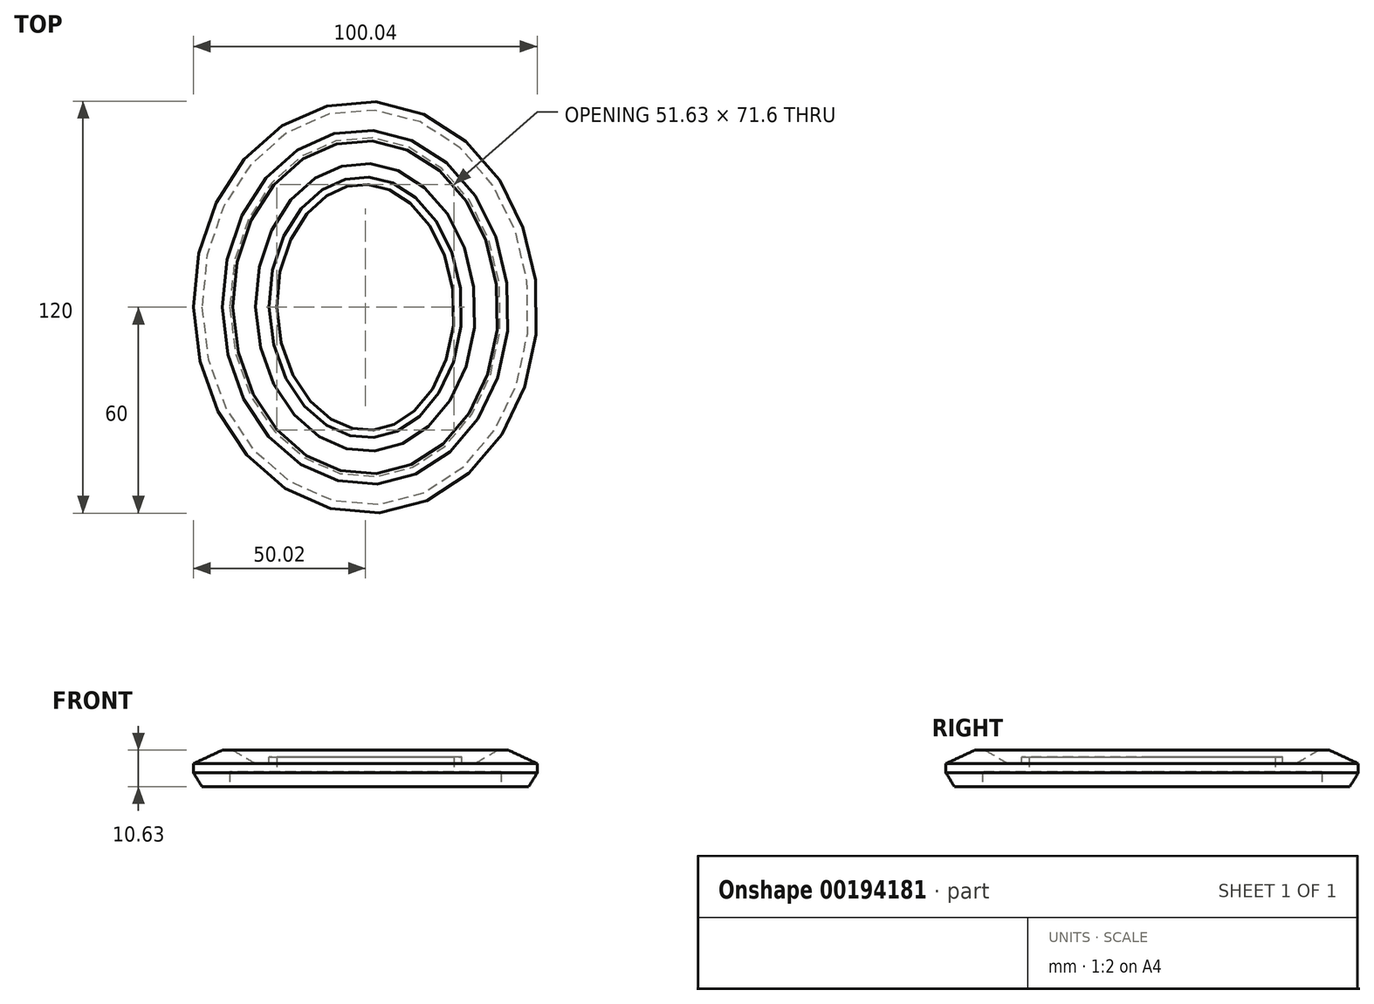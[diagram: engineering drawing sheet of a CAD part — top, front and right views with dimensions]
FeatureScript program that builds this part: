
annotation { "Feature Type Name" : "Feature", "Feature Type Description" : "" }
export const myFeature = defineFeature(function(context is Context, id is Id, definition is map)
    precondition{}
    {
        {
            var Q0;
            Q0=qCreatedBy(makeId("Front.planeOp"),FACE);
            var sketch = newSketch(context, id + "F0", { "sketchPlane" : qUnion([Q0])});
            skLineSegment(sketch, "E0", {"start": v(-47.56, 0.1) * mm, "end": v(-50.02, 4.1) * mm});
            skLineSegment(sketch, "E1", {"start": v(-50.02, 4.1) * mm, "end": v(-50.02, 6.8) * mm});
            skLineSegment(sketch, "E2", {"start": v(-50.02, 6.8) * mm, "end": v(-41.66, 10.73) * mm});
            skLineSegment(sketch, "E3", {"start": v(-41.66, 10.73) * mm, "end": v(-38.6, 10.73) * mm});
            skLineSegment(sketch, "E4", {"start": v(-38.6, 10.73) * mm, "end": v(-31.96, 6.8) * mm});
            skLineSegment(sketch, "E5", {"start": v(-31.96, 6.8) * mm, "end": v(-28.03, 6.8) * mm});
            skLineSegment(sketch, "E6", {"start": v(-28.03, 6.8) * mm, "end": v(-28.03, 8.76) * mm});
            skLineSegment(sketch, "E7", {"start": v(-28.03, 8.76) * mm, "end": v(-25.82, 8.76) * mm});
            skLineSegment(sketch, "E8", {"start": v(-25.82, 8.76) * mm, "end": v(-25.82, 4.43) * mm});
            skLineSegment(sketch, "E9", {"start": v(-25.82, 4.43) * mm, "end": v(-39.46, 4.43) * mm});
            skLineSegment(sketch, "E10", {"start": v(-39.46, 4.43) * mm, "end": v(-39.46, 0.1) * mm});
            skLineSegment(sketch, "E11", {"start": v(-39.46, 0.1) * mm, "end": v(-47.56, 0.1) * mm});
            skSolve(sketch);
        }
        {
            var Q0;
            Q0=qCreatedBy(makeId("Top.planeOp"),FACE);
            var sketch = newSketch(context, id + "F1", { "sketchPlane" : qUnion([Q0])});
            skEllipse(sketch, "E12", {"center": v(0, 0) * mm, "majorRadius": 50 * mm, "minorRadius": 40 * mm, "majorAxis": v(0.03, -1)});
            skSolve(sketch);
        }
        {
            var Q0;
            Q0=makeQuery(id+"F0.imprint","IMPRINT",FACE,{"disambiguationData":[TD([[makeQuery(id+"F0.imprint","IMPRINT",EDGE,{"derivedFrom":sQuery(id+"F0.wireOp",EDGE,"E0")}),-1.0]])]});
            var Q1;
            Q1=sQuery(id+"F1.wireOp",EDGE,"E12");
            sweep(context, id + "F2", {"profiles" : qUnion([Q0]), "path" : qUnion([Q1])});
        }
    });
